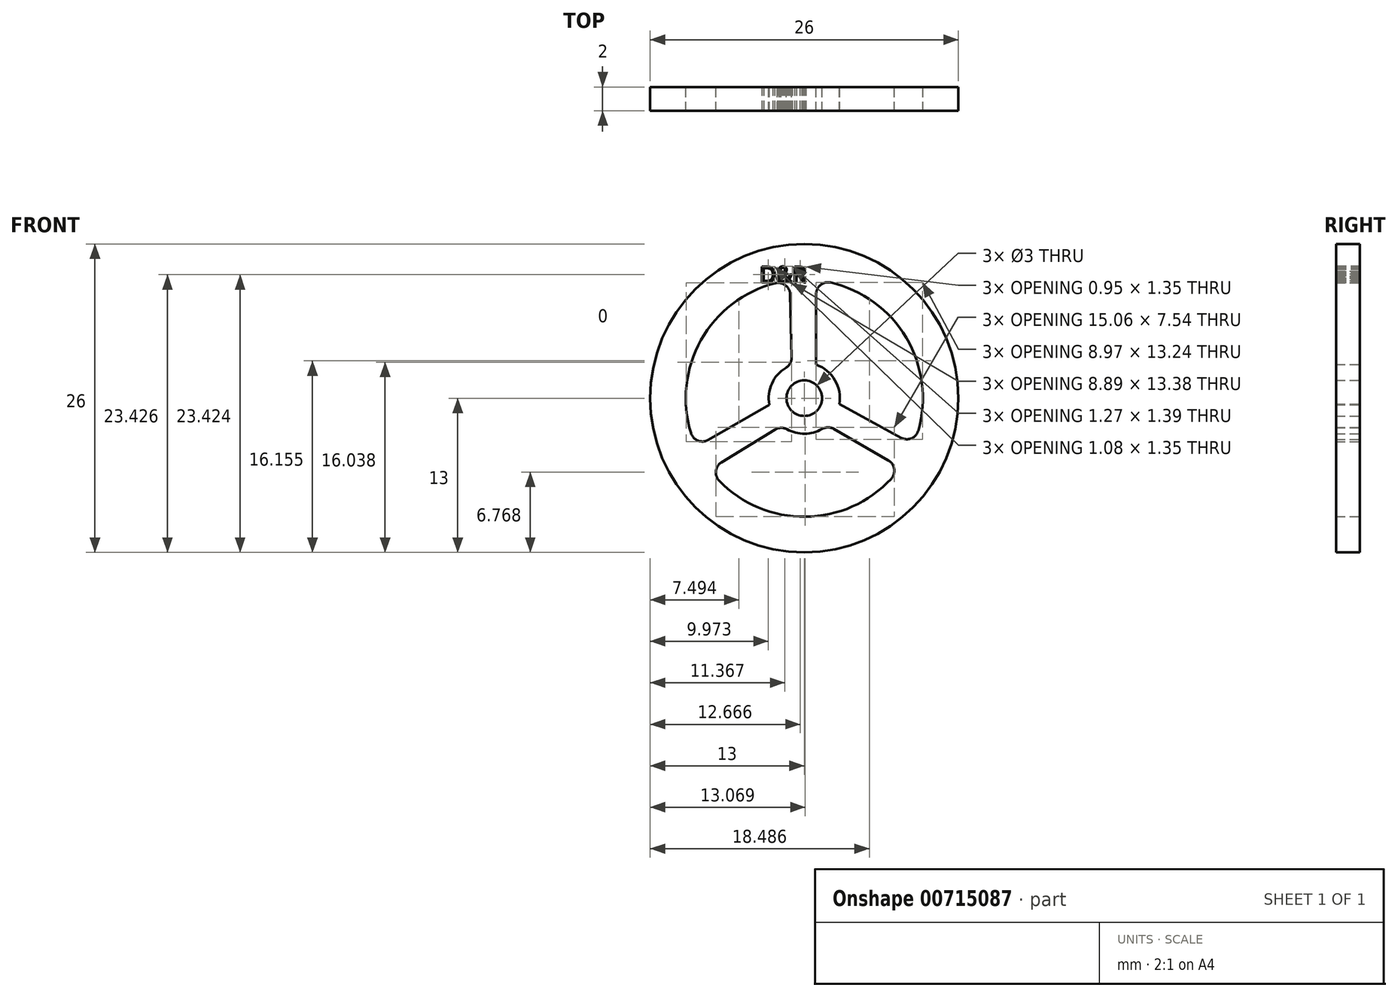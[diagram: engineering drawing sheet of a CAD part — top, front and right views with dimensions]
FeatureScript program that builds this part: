
annotation { "Feature Type Name" : "Feature", "Feature Type Description" : "" }
export const myFeature = defineFeature(function(context is Context, id is Id, definition is map)
    precondition{}
    {
        {
            var Q0;
            Q0=qCreatedBy(makeId("Front.planeOp"),FACE);
            var sketch = newSketch(context, id + "F0", { "sketchPlane" : qUnion([Q0])});
            skArc(sketch, "E0", {"start": v(-2.44, 9.7) * mm, "mid": v(-8.71, 4.9) * mm, "end": v(-9.55, -2.95) * mm});
            skCircle(sketch, "E1.0", {"center": v(0, 0) * mm, "radius": 13 * mm});
            skArc(sketch, "E2", {"start": v(-1.54, 2.57) * mm, "mid": v(-2.74, 1.23) * mm, "end": v(-2.95, -0.55) * mm});
            skCircle(sketch, "E3", {"center": v(0, 0) * mm, "radius": 1.5 * mm});
            skLineSegment(sketch, "E4.0", {"start": v(-1.3, 12.98) * mm, "end": v(-1.3, 12.94) * mm});
            skLineSegment(sketch, "E5.0", {"start": v(1, 13) * mm, "end": v(1, 12.96) * mm});
            skLineSegment(sketch, "E6.trimOffspring", {"start": v(-1.2, 8.75) * mm, "end": v(-1.06, 3.45) * mm});
            skLineSegment(sketch, "E7.trimOffspring", {"start": v(1, 8.77) * mm, "end": v(1, 2.83) * mm});
            skPoint(sketch, "E8.orphan", {"position": v(0, 13) * mm});
            skLineSegment(sketch, "E9.trimOffspring", {"start": v(-1, 1.12) * mm, "end": v(-0.97, -0.1) * mm});
            skLineSegment(sketch, "E10.trimOffspring", {"start": v(1, 1.12) * mm, "end": v(1, 0) * mm});
            skLineSegment(sketch, "E11.1.0", {"start": v(-8.1, -3.52) * mm, "end": v(-2.95, -0.55) * mm});
            skLineSegment(sketch, "E11.1.1", {"start": v(-6.99, -5.4) * mm, "end": v(-2.46, -2.64) * mm});
            skLineSegment(sketch, "E11.2.0", {"start": v(7.1, -5.25) * mm, "end": v(2.5, -2.6) * mm});
            skLineSegment(sketch, "E11.2.1", {"start": v(8.18, -3.34) * mm, "end": v(2.96, -0.5) * mm});
            skArc(sketch, "E12.trimOffspring", {"start": v(-1.46, -2.62) * mm, "mid": v(0.03, -3) * mm, "end": v(1.5, -2.6) * mm});
            skArc(sketch, "E13.trimOffspring", {"start": v(-7.18, -6.96) * mm, "mid": v(0.1, -10) * mm, "end": v(7.33, -6.8) * mm});
            skArc(sketch, "E14.trimOffspring", {"start": v(2.96, -0.5) * mm, "mid": v(2.59, 1.52) * mm, "end": v(1, 2.83) * mm});
            skArc(sketch, "E15.trimOffspring", {"start": v(9.62, -2.74) * mm, "mid": v(8.6, 5.1) * mm, "end": v(2.22, 9.75) * mm});
            skPoint(sketch, "E16.visualSharp", {"position": v(-1.22, 9.93) * mm});
            skArc(sketch, "E16.filletArc", {"start": v(-1.2, 8.75) * mm, "mid": v(-1.59, 9.53) * mm, "end": v(-2.44, 9.7) * mm});
            skPoint(sketch, "E17.visualSharp", {"position": v(-1.04, 2.81) * mm});
            skArc(sketch, "E17.filletArc", {"start": v(-1.54, 2.57) * mm, "mid": v(-1.18, 2.95) * mm, "end": v(-1.06, 3.45) * mm});
            skPoint(sketch, "E18.visualSharp", {"position": v(-9.12, -4.1) * mm});
            skArc(sketch, "E18.filletArc", {"start": v(-9.55, -2.95) * mm, "mid": v(-8.96, -3.59) * mm, "end": v(-8.1, -3.52) * mm});
            skPoint(sketch, "E19.visualSharp", {"position": v(-7.98, -6.02) * mm});
            skArc(sketch, "E19.filletArc", {"start": v(-6.99, -5.4) * mm, "mid": v(-7.46, -6.14) * mm, "end": v(-7.18, -6.96) * mm});
            skPoint(sketch, "E20.visualSharp", {"position": v(1.95, -2.28) * mm});
            skArc(sketch, "E20.filletArc", {"start": v(2.5, -2.6) * mm, "mid": v(2, -2.46) * mm, "end": v(1.5, -2.6) * mm});
            skPoint(sketch, "E21.visualSharp", {"position": v(1, 9.95) * mm});
            skArc(sketch, "E21.filletArc", {"start": v(2.22, 9.75) * mm, "mid": v(1.65, 9.71) * mm, "end": v(1.2, 9.37) * mm});
            skPoint(sketch, "E22.visualSharp", {"position": v(9.2, -3.9) * mm});
            skArc(sketch, "E22.filletArc", {"start": v(8.18, -3.34) * mm, "mid": v(9.04, -3.39) * mm, "end": v(9.62, -2.74) * mm});
            skPoint(sketch, "E23.visualSharp", {"position": v(8.12, -5.84) * mm});
            skArc(sketch, "E23.filletArc", {"start": v(7.33, -6.8) * mm, "mid": v(7.59, -5.97) * mm, "end": v(7.1, -5.25) * mm});
            skPoint(sketch, "E24.visualSharp", {"position": v(-1.91, -2.3) * mm});
            skArc(sketch, "E24.filletArc", {"start": v(-1.46, -2.62) * mm, "mid": v(-1.96, -2.5) * mm, "end": v(-2.46, -2.64) * mm});
            skPoint(sketch, "E25.visualSharp", {"position": v(1, 8.77) * mm});
            skArc(sketch, "E25.filletArc", {"start": v(1.2, 9.37) * mm, "mid": v(1.05, 9.09) * mm, "end": v(1, 8.77) * mm});
            skSolve(sketch);
        }
        {
            var Q0;
            Q0=makeQuery(id+"F0.imprint","IMPRINT",FACE,{"disambiguationData":[TD([[makeQuery(id+"F0.imprint","IMPRINT",EDGE,{"derivedFrom":sQuery(id+"F0.wireOp",EDGE,"E0")}),-1.0]])]});
            extrude(context, id + "F1", {"entities" : qUnion([Q0]), "depth" : 2 * mm, "offsetDistance" : 25 * mm, "symmetric" : true});
        }
        {
            var Q0;
            Q0=makeQuery(id+"F1.opExtrude","CAP_FACE",FACE,{"disambiguationData":[OSD([sQuery(id+"F0.wireOp",EDGE,"E0"),sQuery(id+"F0.wireOp",EDGE,"E1.0"),sQuery(id+"F0.wireOp",EDGE,"E2"),sQuery(id+"F0.wireOp",EDGE,"E3"),sQuery(id+"F0.wireOp",EDGE,"E6.trimOffspring"),sQuery(id+"F0.wireOp",EDGE,"E7.trimOffspring"),sQuery(id+"F0.wireOp",EDGE,"E11.1.0"),sQuery(id+"F0.wireOp",EDGE,"E11.1.1"),sQuery(id+"F0.wireOp",EDGE,"E11.2.0"),sQuery(id+"F0.wireOp",EDGE,"E11.2.1"),sQuery(id+"F0.wireOp",EDGE,"E12.trimOffspring"),sQuery(id+"F0.wireOp",EDGE,"E13.trimOffspring"),sQuery(id+"F0.wireOp",EDGE,"E14.trimOffspring"),sQuery(id+"F0.wireOp",EDGE,"E15.trimOffspring"),sQuery(id+"F0.wireOp",EDGE,"E16.filletArc"),sQuery(id+"F0.wireOp",EDGE,"E17.filletArc"),sQuery(id+"F0.wireOp",EDGE,"E18.filletArc"),sQuery(id+"F0.wireOp",EDGE,"E19.filletArc"),sQuery(id+"F0.wireOp",EDGE,"E20.filletArc"),sQuery(id+"F0.wireOp",EDGE,"E21.filletArc"),sQuery(id+"F0.wireOp",EDGE,"E22.filletArc"),sQuery(id+"F0.wireOp",EDGE,"E23.filletArc"),sQuery(id+"F0.wireOp",EDGE,"E24.filletArc"),sQuery(id+"F0.wireOp",EDGE,"E25.filletArc")])],"isStart":false});
            var sketch = newSketch(context, id + "F2", { "sketchPlane" : qUnion([Q0])});
            skText(sketch, "E26", { "text": "D&R", "fontName": "OpenSans-Regular.ttf"});
            const initialGuessF2  = {"E26": [-0.00375, 0.00975, 1, 0, 0.00136]};
            skSetInitialGuess(sketch, initialGuessF2);
            skSolve(sketch);
        }
        {
            var Q0;
            Q0 = qSketchRegion(id + "F2", true);
            extrude(context, id + "F3", {"entities" : qUnion([Q0]), "operationType" : NewBodyOperationType.REMOVE, "oppositeDirection" : true, "depth" : 25.4 * mm, "offsetDistance" : 25.4 * mm});
        }
    });
